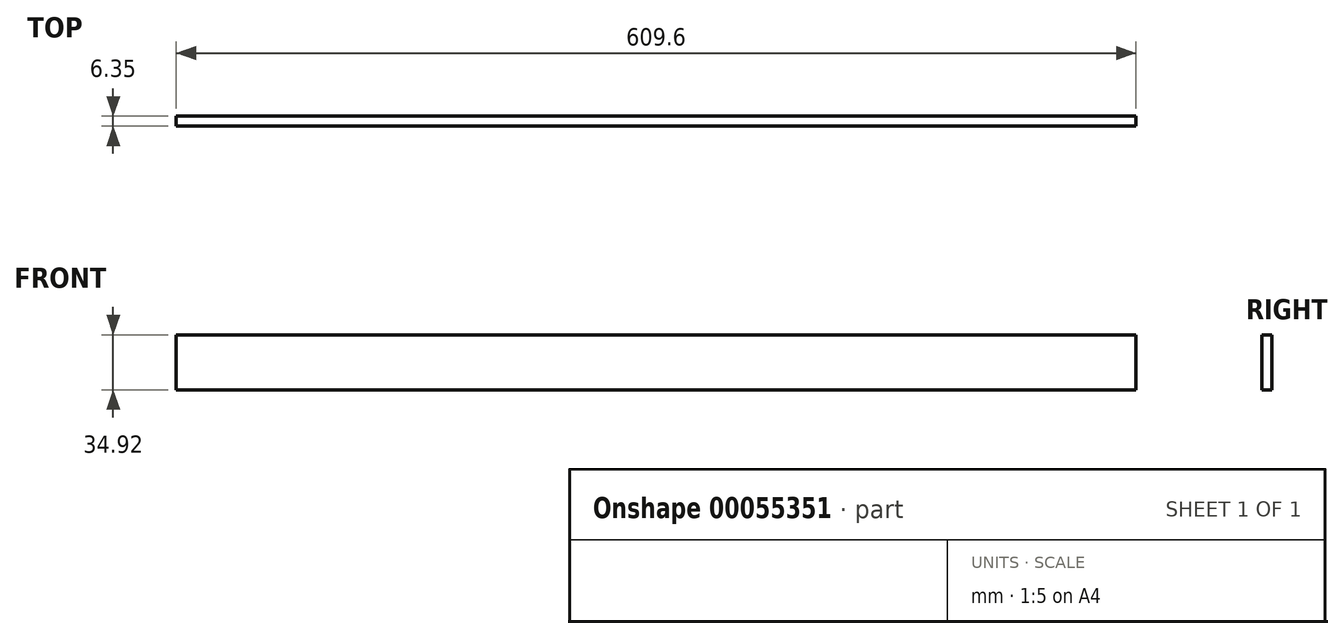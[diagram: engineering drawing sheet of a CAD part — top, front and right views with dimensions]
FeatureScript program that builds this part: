
annotation { "Feature Type Name" : "Feature", "Feature Type Description" : "" }
export const myFeature = defineFeature(function(context is Context, id is Id, definition is map)
    precondition{}
    {
        {
            var Q0;
            Q0=qCreatedBy(makeId("Front.planeOp"),FACE);
            var sketch = newSketch(context, id + "F0", { "sketchPlane" : qUnion([Q0])});
            skLineSegment(sketch, "E0.bottom", {"start": v(0, 0) * mm, "end": v(609.6, 0) * mm});
            skLineSegment(sketch, "E0.top", {"start": v(0, 34.93) * mm, "end": v(609.6, 34.93) * mm});
            skLineSegment(sketch, "E0.left", {"start": v(0, 0) * mm, "end": v(0, 34.93) * mm});
            skLineSegment(sketch, "E0.right", {"start": v(609.6, 0) * mm, "end": v(609.6, 34.93) * mm});
            skSolve(sketch);
        }
        {
            var Q0;
            Q0 = qSketchRegion(id + "F0", true);
            extrude(context, id + "F1", {"entities" : qUnion([Q0]), "depth" : 6.35 * mm});
        }
    });
